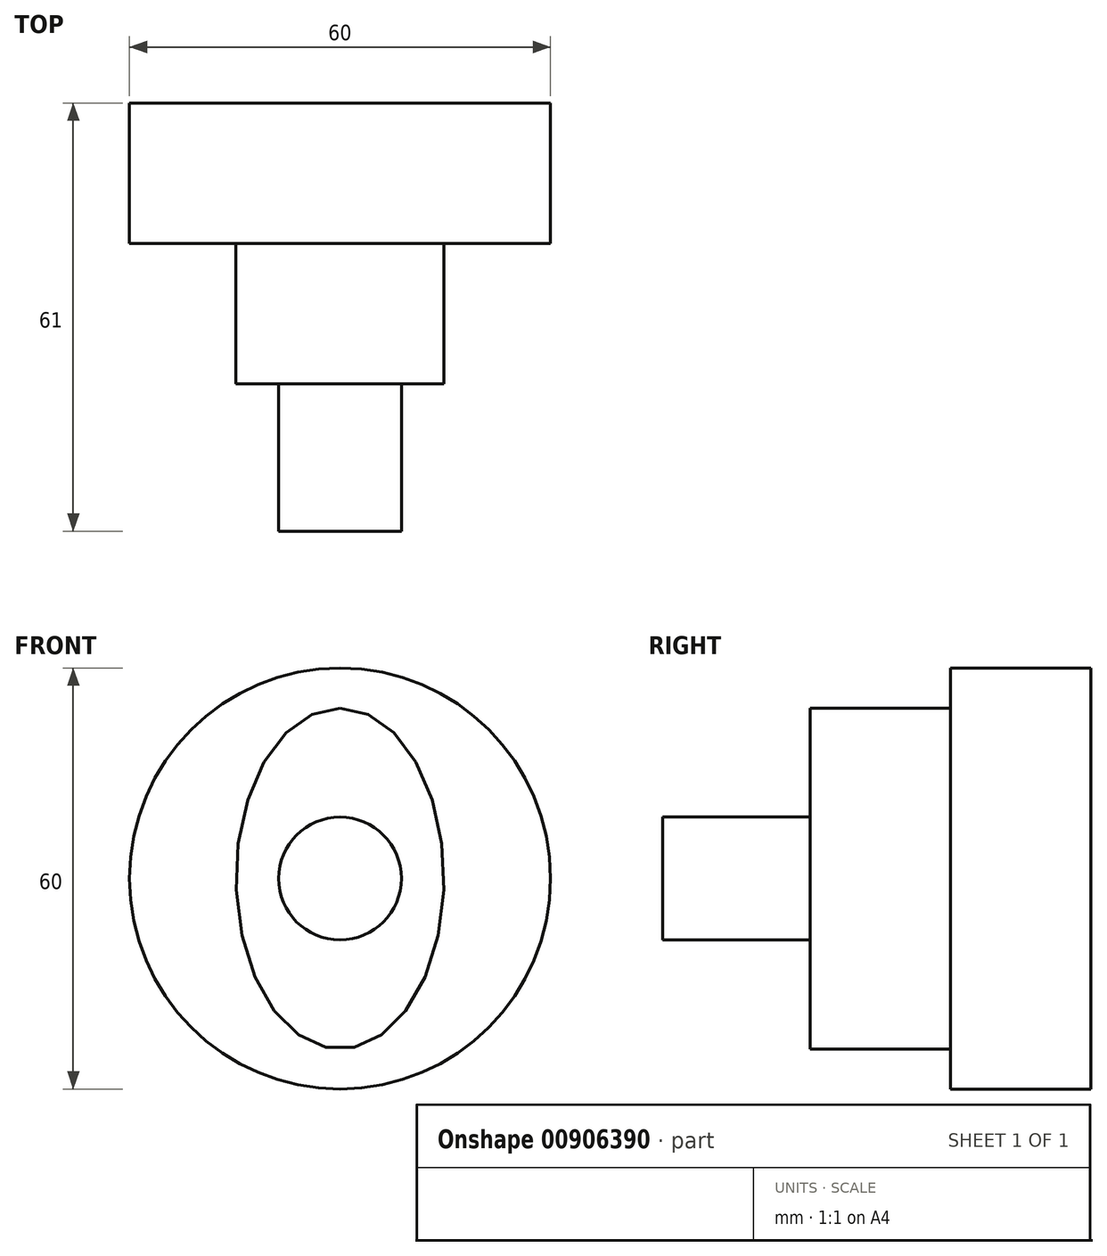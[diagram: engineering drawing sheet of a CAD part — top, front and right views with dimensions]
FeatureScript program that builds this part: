
annotation { "Feature Type Name" : "Feature", "Feature Type Description" : "" }
export const myFeature = defineFeature(function(context is Context, id is Id, definition is map)
    precondition{}
    {
        {
            var Q0;
            Q0=qCreatedBy(makeId("Front.planeOp"),FACE);
            var sketch = newSketch(context, id + "F0", { "sketchPlane" : qUnion([Q0])});
            skCircle(sketch, "E0", {"center": v(0, 0) * mm, "radius": 30 * mm});
            skSolve(sketch);
        }
        {
            var Q0;
            Q0=makeQuery(id+"F0.imprint","IMPRINT",FACE,{"disambiguationData":[TD([[makeQuery(id+"F0.imprint","IMPRINT",EDGE,{"derivedFrom":sQuery(id+"F0.wireOp",EDGE,"E0")}),1.0]])]});
            extrude(context, id + "F1", {"entities" : qUnion([Q0]), "depth" : 20 * mm, "offsetDistance" : 25 * mm});
        }
        {
            var Q0;
            Q0=makeQuery(id+"F1.opExtrude","CAP_FACE",FACE,{"disambiguationData":[OSD([sQuery(id+"F0.wireOp",EDGE,"E0")])],"isStart":false});
            var sketch = newSketch(context, id + "F2", { "sketchPlane" : qUnion([Q0])});
            skEllipse(sketch, "E1", {"center": v(0, 0) * mm, "majorRadius": 24.3 * mm, "minorRadius": 14.82 * mm, "majorAxis": v(0, 1)});
            skSolve(sketch);
        }
        {
            var Q0;
            Q0 = qSketchRegion(id + "F2", true);
            extrude(context, id + "F3", {"entities" : qUnion([Q0]), "operationType" : NewBodyOperationType.ADD, "depth" : 20 * mm, "offsetDistance" : 25 * mm});
        }
        {
            var Q0;
            Q0=makeQuery(id+"F3.opExtrude","CAP_FACE",FACE,{"disambiguationData":[OSD([sQuery(id+"F2.wireOp",EDGE,"E1")])],"isStart":false});
            var sketch = newSketch(context, id + "F4", { "sketchPlane" : qUnion([Q0])});
            skCircle(sketch, "E2", {"center": v(0, 0) * mm, "radius": 8.75 * mm});
            skSolve(sketch);
        }
        {
            var Q0;
            Q0 = qSketchRegion(id + "F4", true);
            extrude(context, id + "F5", {"entities" : qUnion([Q0]), "operationType" : NewBodyOperationType.ADD, "depth" : 21 * mm, "offsetDistance" : 25 * mm});
        }
    });
